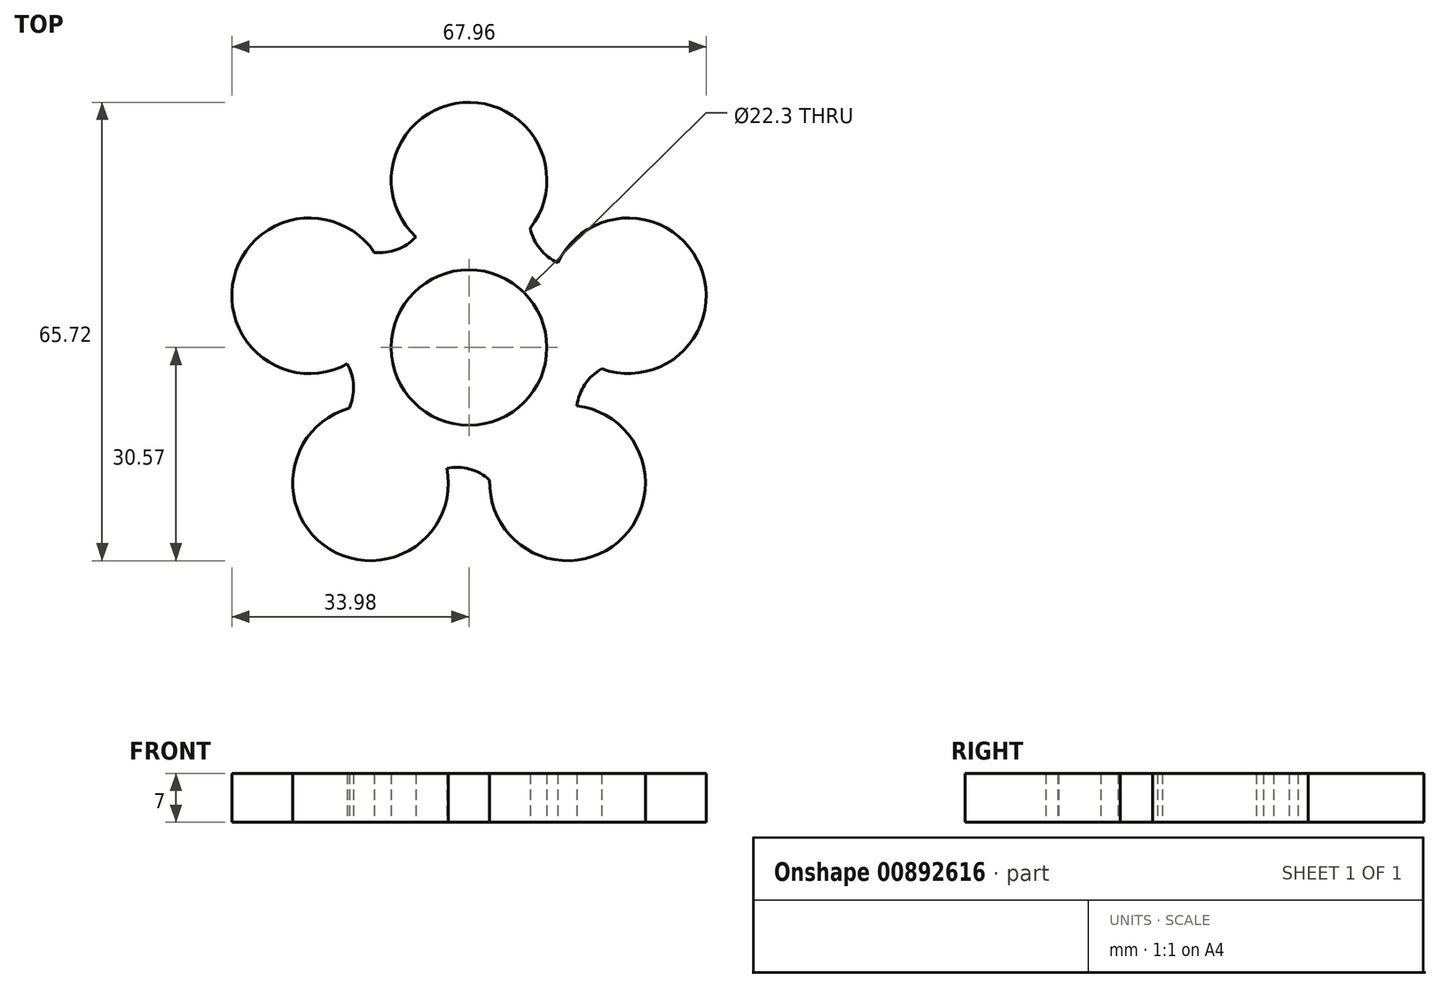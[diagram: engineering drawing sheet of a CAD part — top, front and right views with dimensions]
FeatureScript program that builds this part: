
annotation { "Feature Type Name" : "Feature", "Feature Type Description" : "" }
export const myFeature = defineFeature(function(context is Context, id is Id, definition is map)
    precondition{}
    {
        {
            var Q0;
            Q0=qCreatedBy(makeId("Top.planeOp"),FACE);
            var sketch = newSketch(context, id + "F0", { "sketchPlane" : qUnion([Q0])});
            skCircle(sketch, "E0", {"center": v(0, 0) * mm, "radius": 11.15 * mm});
            skArc(sketch, "E1", {"start": v(8.77, 17.12) * mm, "mid": v(-0.86, 35.12) * mm, "end": v(-7.6, 15.85) * mm});
            skArc(sketch, "E2.1.0", {"start": v(-13.57, 13.63) * mm, "mid": v(-33.66, 10.03) * mm, "end": v(-17.42, -2.34) * mm});
            skArc(sketch, "E2.2.0", {"start": v(-17.16, -8.7) * mm, "mid": v(-19.94, -28.92) * mm, "end": v(-3.16, -17.3) * mm});
            skArc(sketch, "E2.3.0", {"start": v(2.96, -19) * mm, "mid": v(21.34, -27.9) * mm, "end": v(15.47, -8.35) * mm});
            skArc(sketch, "E2.4.0", {"start": v(18.99, -3.05) * mm, "mid": v(33.13, 11.67) * mm, "end": v(12.72, 12.13) * mm});
            skLineSegment(sketch, "E3", {"start": v(0, 24) * mm, "end": v(11.15, 24) * mm});
            skLineSegment(sketch, "E4", {"start": v(22.83, 7.42) * mm, "end": v(22.83, 18.57) * mm, "construction": true});
            skArc(sketch, "E5", {"start": v(8.77, 17.12) * mm, "mid": v(10.16, 14.16) * mm, "end": v(12.72, 12.13) * mm});
            skArc(sketch, "E6.1.0", {"start": v(-13.57, 13.63) * mm, "mid": v(-10.32, 14.03) * mm, "end": v(-7.6, 15.85) * mm});
            skArc(sketch, "E6.2.0", {"start": v(-17.16, -8.7) * mm, "mid": v(-16.54, -5.48) * mm, "end": v(-17.42, -2.34) * mm});
            skArc(sketch, "E6.3.0", {"start": v(2.96, -19) * mm, "mid": v(0.1, -17.42) * mm, "end": v(-3.16, -17.3) * mm});
            skArc(sketch, "E6.4.0", {"start": v(18.99, -3.05) * mm, "mid": v(16.6, -5.28) * mm, "end": v(15.47, -8.35) * mm});
            skSolve(sketch);
        }
        {
            var Q0;
            Q0=makeQuery(id+"F0.imprint","IMPRINT",FACE,{"disambiguationData":[TD([[makeQuery(id+"F0.imprint","IMPRINT",EDGE,{"derivedFrom":sQuery(id+"F0.wireOp",EDGE,"E0")}),-1.0]])]});
            extrude(context, id + "F1", {"entities" : qUnion([Q0]), "depth" : 7 * mm, "offsetDistance" : 25 * mm});
        }
    });
